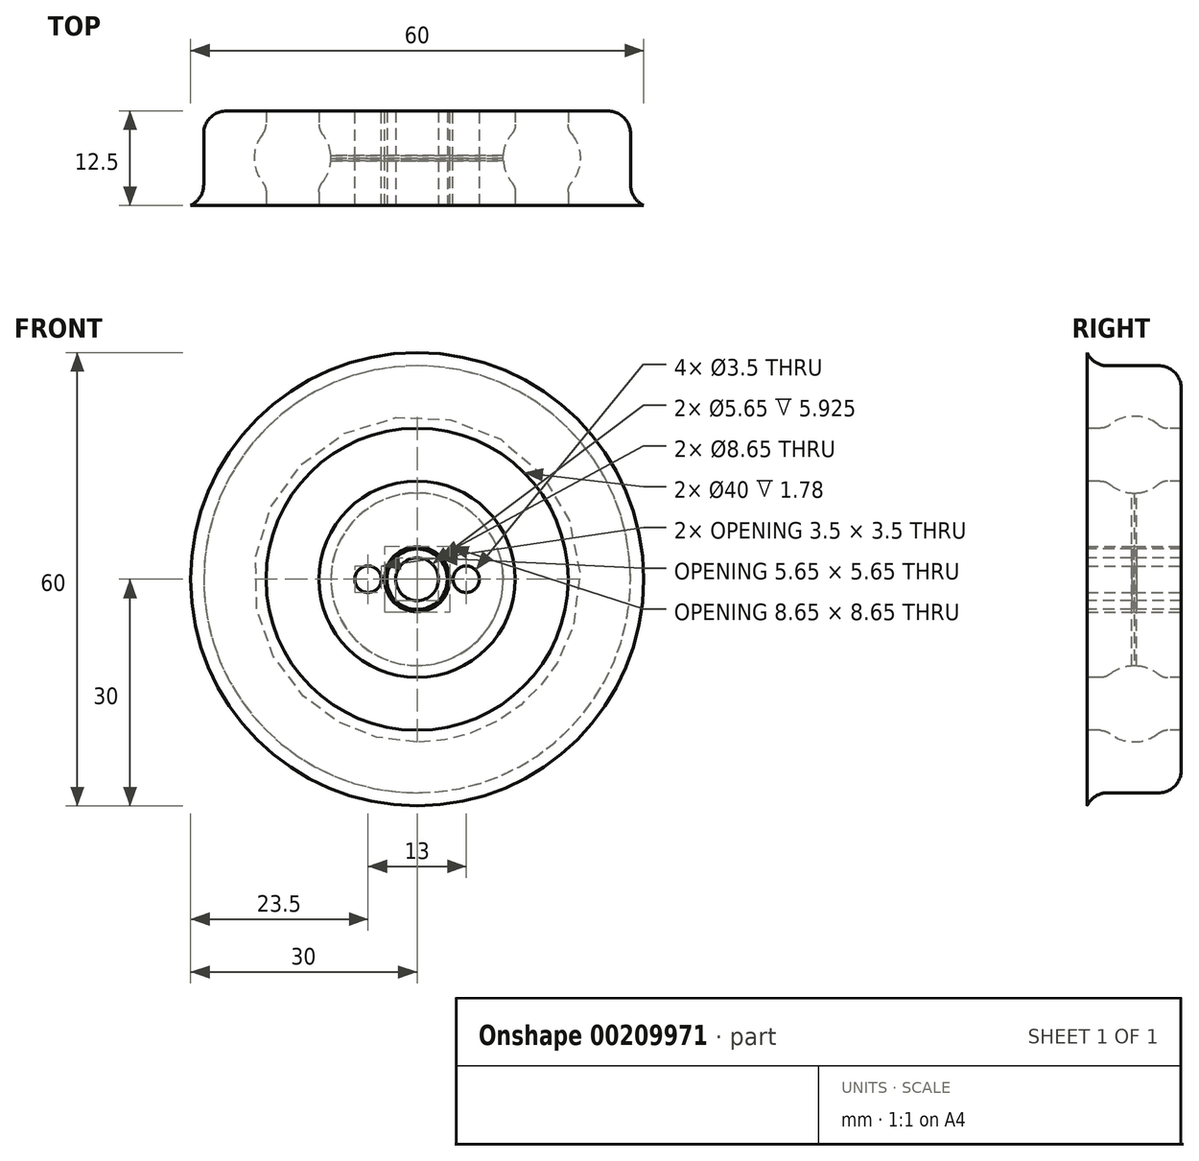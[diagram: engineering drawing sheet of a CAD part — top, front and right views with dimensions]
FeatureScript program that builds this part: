
annotation { "Feature Type Name" : "Feature", "Feature Type Description" : "" }
export const myFeature = defineFeature(function(context is Context, id is Id, definition is map)
    precondition{}
    {
        {
            var Q0;
            Q0=qCreatedBy(makeId("Top.planeOp"),FACE);
            var sketch = newSketch(context, id + "F0", { "sketchPlane" : qUnion([Q0])});
            skLineSegment(sketch, "E0", {"start": v(0, 0) * mm, "end": v(0, 12.5) * mm});
            skLineSegment(sketch, "E1", {"start": v(-28.27, 12.5) * mm, "end": v(-28.27, 1) * mm});
            skLineSegment(sketch, "E2", {"start": v(-28.27, 1) * mm, "end": v(-30, 0) * mm});
            skLineSegment(sketch, "E3", {"start": v(-30, 0) * mm, "end": v(0, 0) * mm});
            skCircle(sketch, "E4", {"center": v(-16.5, 6.25) * mm, "radius": 5.09 * mm});
            skPoint(sketch, "E4.centerSnap0", {"position": v(0, 6.25) * mm});
            skCircle(sketch, "E5", {"center": v(-16.5, 6.25) * mm, "radius": 4.76 * mm, "construction": true});
            skLineSegment(sketch, "E6", {"start": v(-20, 9.94) * mm, "end": v(-20, 12.5) * mm});
            skLineSegment(sketch, "E7", {"start": v(-13, 9.94) * mm, "end": v(-13, 12.5) * mm});
            skLineSegment(sketch, "E8", {"start": v(-20, 2.56) * mm, "end": v(-20, 0) * mm});
            skLineSegment(sketch, "E9", {"start": v(-13, 2.56) * mm, "end": v(-13, 0) * mm});
            skLineSegment(sketch, "E10", {"start": v(-2.83, 12.5) * mm, "end": v(-2.82, 0) * mm});
            skLineSegment(sketch, "E11", {"start": v(-4, 12.5) * mm, "end": v(-4, 6.25) * mm});
            skLineSegment(sketch, "E12", {"start": v(-4, 6.25) * mm, "end": v(-11.41, 6.25) * mm});
            skLineSegment(sketch, "E13", {"start": v(-28.27, 12.5) * mm, "end": v(0, 12.5) * mm});
            skSolve(sketch);
        }
        {
            var Q0;
            {var subQ4=sQuery(id+"F0.wireOp",EDGE,"E1");Q0=makeQuery(id+"F0.imprint","IMPRINT",FACE,{"disambiguationData":[TD([[makeQuery(id+"F0.imprint","IMPRINT",EDGE,{"derivedFrom":subQ4}),1.0]])]});}
            var Q1;
            {var subQ0=sQuery(id+"F0.wireOp",EDGE,"E7");Q1=makeQuery(id+"F0.imprint","IMPRINT",FACE,{"disambiguationData":[TD([[makeQuery(id+"F0.imprint","IMPRINT",EDGE,{"derivedFrom":subQ0}),-1.0]])]});}
            var Q2;
            Q2=sQuery(id+"F0.wireOp",EDGE,"E0");
            revolve(context, id + "F1", {"entities" : qUnion([Q0, Q1]), "axis" : qUnion([Q2]), "revolveType" : RevolveType.FULL});
        }
        {
            var Q0;
            {var subQ5=sQuery(id+"F0.wireOp",EDGE,"E9");Q0=makeQuery(id+"F0.imprint","IMPRINT",FACE,{"disambiguationData":[TD([[makeQuery(id+"F0.imprint","IMPRINT",EDGE,{"derivedFrom":subQ5}),1.0]])]});}
            var Q1;
            Q1=sQuery(id+"F0.wireOp",EDGE,"E0");
            revolve(context, id + "F2", {"entities" : qUnion([Q0]), "axis" : qUnion([Q1]), "revolveType" : RevolveType.FULL});
        }
        {
            var Q0;
            {var subQ0=sQuery(id+"F0.wireOp",EDGE,"E13");Q0=makeQuery(id+"F1.opRevolve","SWEPT_FACE",FACE,{"disambiguationData":[OSD([subQ0]),TDD([makeQuery(id+"F0.imprint","IMPRINT",EDGE,{"disambiguationData":[TD([[makeQuery(id+"F0.imprint","INTERSECT",VERTEX,{"derivedFrom":[sQuery(id+"F0.wireOp",EDGE,"E7"),subQ0]}),-1.0]])],"derivedFrom":subQ0})])]});}
            var sketch = newSketch(context, id + "F3", { "sketchPlane" : qUnion([Q0])});
            skLineSegment(sketch, "E14", {"start": v(0, 0) * mm, "end": v(-6.5, 0) * mm});
            skLineSegment(sketch, "E15", {"start": v(0, 0) * mm, "end": v(6.5, 0) * mm});
            skCircle(sketch, "E16", {"center": v(-6.5, 0) * mm, "radius": 1.75 * mm});
            skCircle(sketch, "E17", {"center": v(6.5, 0) * mm, "radius": 1.75 * mm});
            skCircle(sketch, "E18", {"center": v(0, 0) * mm, "radius": 4.33 * mm});
            skSolve(sketch);
        }
        {
            var Q0;
            Q0=makeQuery(id+"F3.imprint","IMPRINT",FACE,{"disambiguationData":[TD([[makeQuery(id+"F3.imprint","IMPRINT",EDGE,{"derivedFrom":sQuery(id+"F3.wireOp",EDGE,"E16")}),1.0]])]});
            var Q1;
            Q1=makeQuery(id+"F3.imprint","IMPRINT",FACE,{"disambiguationData":[TD([[makeQuery(id+"F3.imprint","IMPRINT",EDGE,{"derivedFrom":sQuery(id+"F3.wireOp",EDGE,"E17")}),1.0]])]});
            extrude(context, id + "F4", {"entities" : qUnion([Q0, Q1]), "operationType" : NewBodyOperationType.REMOVE, "oppositeDirection" : true, "depth" : 25 * mm});
        }
        {
            var Q0;
            {var subQ0=sQuery(id+"F3.wireOp",EDGE,"E18");var subQ1=sQuery(id+"F3.wireOp",EDGE,"E14");var subQ2=makeQuery(id+"F3.imprint","INTERSECT",VERTEX,{"derivedFrom":[subQ1,subQ0]});Q0=makeQuery(id+"F3.imprint","IMPRINT",FACE,{"disambiguationData":[TD([[makeQuery(id+"F3.imprint","IMPRINT",EDGE,{"disambiguationData":[TD([[subQ2,-1.0]])],"derivedFrom":subQ0}),1.0]])]});}
            var Q1;
            {var subQ0=sQuery(id+"F3.wireOp",EDGE,"E18");var subQ1=sQuery(id+"F3.wireOp",EDGE,"E14");var subQ2=makeQuery(id+"F3.imprint","INTERSECT",VERTEX,{"derivedFrom":[subQ1,subQ0]});Q1=makeQuery(id+"F3.imprint","IMPRINT",FACE,{"disambiguationData":[TD([[makeQuery(id+"F3.imprint","IMPRINT",EDGE,{"disambiguationData":[TD([[subQ2,1.0]])],"derivedFrom":subQ0}),1.0]])]});}
            extrude(context, id + "F5", {"entities" : qUnion([Q0, Q1]), "operationType" : NewBodyOperationType.REMOVE, "oppositeDirection" : true, "depth" : 25 * mm});
        }
        {
            var Q0;
            Q0=makeQuery(id+"F1.opRevolve","SWEPT_EDGE",EDGE,{"disambiguationData":[OSD([sQuery(id+"F0.wireOp",EDGE,"WCJs0gnF-bmEq-8Mfy-u8EZ-gVu7e8cmiNRk"),sQuery(id+"F0.wireOp",EDGE,"E1")])]});
            var Q1;
            Q1=makeQuery(id+"F1.opRevolve","SWEPT_EDGE",EDGE,{"disambiguationData":[OSD([sQuery(id+"F0.wireOp",EDGE,"E1"),sQuery(id+"F0.wireOp",EDGE,"E2")])]});
            fillet(context, id + "F6", {"entities" : qUnion([Q0, Q1]), "radius" : 3 * mm, "tangentPropagation" : true, "allowEdgeOverflow" : false});
        }
        {
            var Q0;
            Q0=makeQuery(id+"F1.opRevolve","SWEPT_EDGE",EDGE,{"disambiguationData":[OSD([sQuery(id+"F0.wireOp",EDGE,"E4"),sQuery(id+"F0.wireOp",EDGE,"E8")])]});
            var Q1;
            Q1=makeQuery(id+"F1.opRevolve","SWEPT_EDGE",EDGE,{"disambiguationData":[OSD([sQuery(id+"F0.wireOp",EDGE,"E4"),sQuery(id+"F0.wireOp",EDGE,"E6")])]});
            var Q2;
            Q2=makeQuery(id+"F1.opRevolve","SWEPT_EDGE",EDGE,{"disambiguationData":[OSD([sQuery(id+"F0.wireOp",EDGE,"E4"),sQuery(id+"F0.wireOp",EDGE,"E7")])]});
            var Q3;
            Q3=makeQuery(id+"F2.opRevolve","SWEPT_EDGE",EDGE,{"disambiguationData":[OSD([sQuery(id+"F0.wireOp",EDGE,"E4"),sQuery(id+"F0.wireOp",EDGE,"E9")])]});
            fillet(context, id + "F7", {"entities" : qUnion([Q0, Q1, Q2, Q3]), "radius" : 2 * mm, "tangentPropagation" : true, "allowEdgeOverflow" : false});
        }
        {
            var Q0;
            Q0=makeQuery(id+"F2.opRevolve","SWEPT_FACE",FACE,{"disambiguationData":[OSD([sQuery(id+"F0.wireOp",EDGE,"E12")])]});
            var sketch = newSketch(context, id + "F8", { "sketchPlane" : qUnion([Q0])});
            skCircle(sketch, "E19", {"center": v(0, 0) * mm, "radius": 4 * mm});
            skCircle(sketch, "E20", {"center": v(0, 0) * mm, "radius": 12.5 * mm});
            skSolve(sketch);
        }
        {
            var Q0;
            Q0=makeQuery(id+"F8.imprint","IMPRINT",FACE,{"disambiguationData":[TD([[makeQuery(id+"F8.imprint","IMPRINT",EDGE,{"derivedFrom":sQuery(id+"F8.wireOp",EDGE,"E19")}),1.0]])]});
            var Q1;
            Q1=makeQuery(id+"F8.imprint","IMPRINT",FACE,{"disambiguationData":[TD([[makeQuery(id+"F8.imprint","IMPRINT",EDGE,{"derivedFrom":sQuery(id+"F8.wireOp",EDGE,"E20")}),1.0]])]});
            extrude(context, id + "F9", {"entities" : qUnion([Q0, Q1]), "operationType" : NewBodyOperationType.REMOVE, "endBound" : BoundingType.SYMMETRIC, "oppositeDirection" : true, "depth" : .65 * mm});
        }
    });
